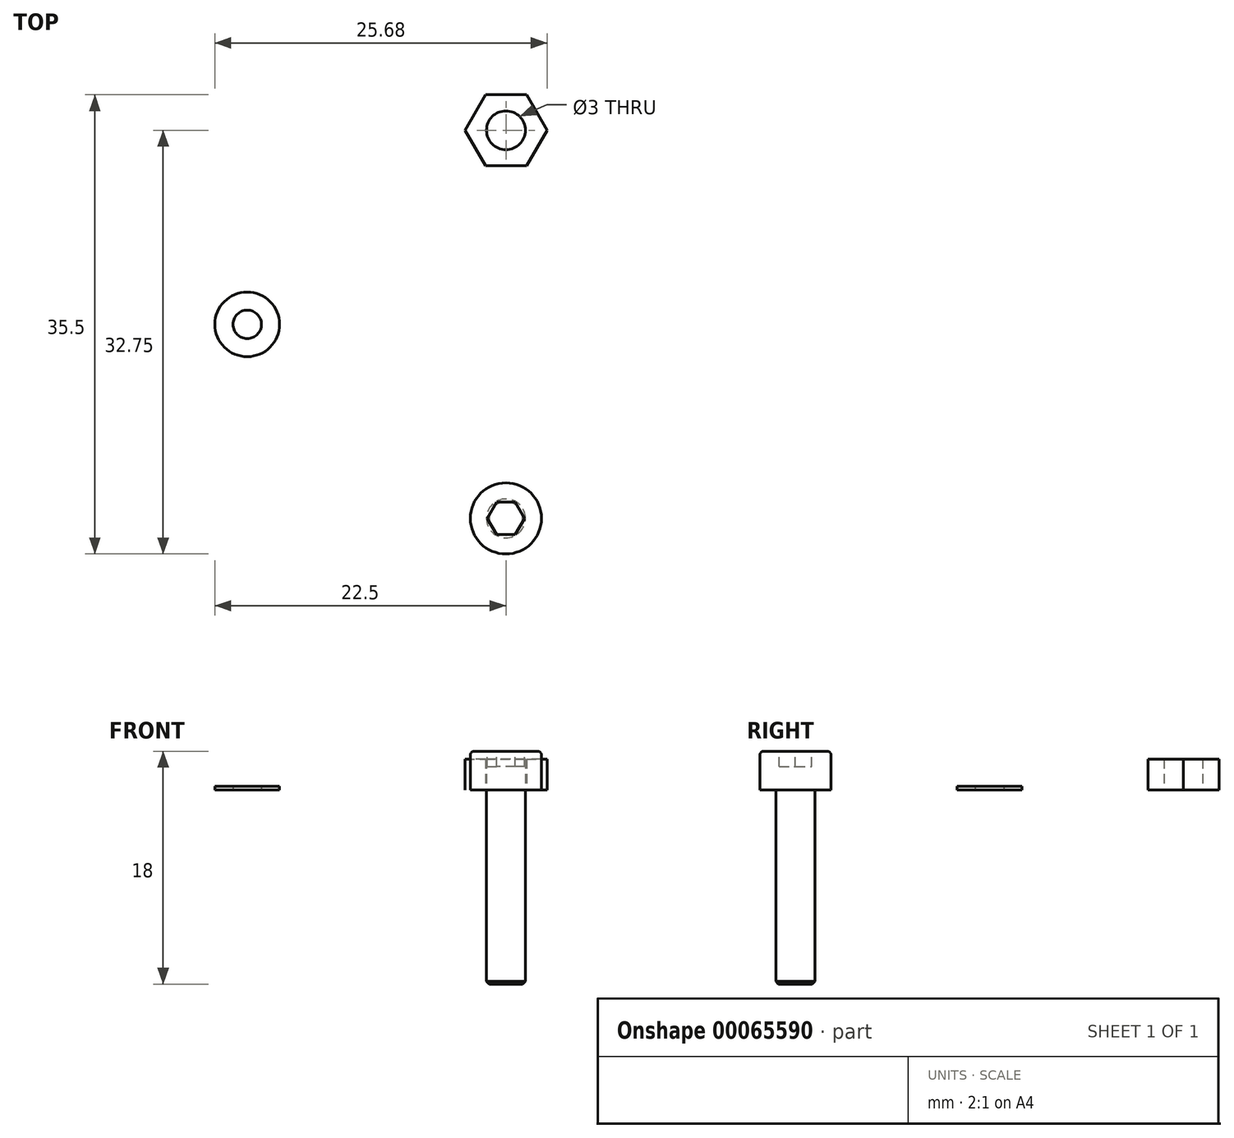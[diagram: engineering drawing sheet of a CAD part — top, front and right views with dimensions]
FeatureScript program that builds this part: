
annotation { "Feature Type Name" : "Feature", "Feature Type Description" : "" }
export const myFeature = defineFeature(function(context is Context, id is Id, definition is map)
    precondition{}
    {
        {
            var Q0;
            Q0=qCreatedBy(makeId("Front.planeOp"),FACE);
            var sketch = newSketch(context, id + "F0", { "sketchPlane" : qUnion([Q0])});
            skLineSegment(sketch, "E0", {"start": v(-10, -10.01) * mm, "end": v(-10, 8.31) * mm, "construction": true});
            skLineSegment(sketch, "E1", {"start": v(-10, 0) * mm, "end": v(-12.75, 0) * mm});
            skLineSegment(sketch, "E2", {"start": v(-12.75, 0) * mm, "end": v(-12.75, 3) * mm});
            skLineSegment(sketch, "E3", {"start": v(-12.75, 3) * mm, "end": v(-10, 3) * mm});
            skLineSegment(sketch, "E4", {"start": v(-10, 3) * mm, "end": v(-10, 0) * mm});
            skLineSegment(sketch, "E5", {"start": v(-10, 0) * mm, "end": v(-10, -15) * mm});
            skLineSegment(sketch, "E6", {"start": v(-10, -15) * mm, "end": v(-11.5, -15) * mm});
            skLineSegment(sketch, "E7", {"start": v(-11.5, -15) * mm, "end": v(-11.5, 0) * mm});
            skSolve(sketch);
        }
        {
            var Q0;
            {var subQ0=sQuery(id+"F0.wireOp",EDGE,"E5");Q0=makeQuery(id+"F0.imprint","IMPRINT",FACE,{"disambiguationData":[TD([[makeQuery(id+"F0.imprint","IMPRINT",EDGE,{"derivedFrom":subQ0}),-1.0]])]});}
            var Q1;
            {var subQ1=sQuery(id+"F0.wireOp",EDGE,"E2");Q1=makeQuery(id+"F0.imprint","IMPRINT",FACE,{"disambiguationData":[TD([[makeQuery(id+"F0.imprint","IMPRINT",EDGE,{"derivedFrom":subQ1}),-1.0]])]});}
            var Q2;
            Q2=sQuery(id+"F0.wireOp",EDGE,"E0");
            revolve(context, id + "F1", {"entities" : qUnion([Q0, Q1]), "axis" : qUnion([Q2]), "revolveType" : RevolveType.FULL});
        }
        {
            var Q0;
            Q0=makeQuery(id+"F1.opRevolve","SWEPT_EDGE",EDGE,{"disambiguationData":[OSD([sQuery(id+"F0.wireOp",EDGE,"E2"),sQuery(id+"F0.wireOp",EDGE,"E3")])]});
            fillet(context, id + "F2", {"entities" : qUnion([Q0]), "radius" : 0.3 * mm, "tangentPropagation" : true, "allowEdgeOverflow" : false});
        }
        {
            var Q0;
            Q0=makeQuery(id+"F1.opRevolve","SWEPT_FACE",FACE,{"disambiguationData":[OSD([sQuery(id+"F0.wireOp",EDGE,"E3")])]});
            var sketch = newSketch(context, id + "F3", { "sketchPlane" : qUnion([Q0])});
            skCircle(sketch, "E8.cCircle", {"center": v(-10, 0) * mm, "radius": 1.25 * mm, "construction": true});
            skLineSegment(sketch, "E8.0", {"start": v(-11.44, 0) * mm, "end": v(-10.72, 1.25) * mm});
            skLineSegment(sketch, "E8.1", {"start": v(-10.72, 1.25) * mm, "end": v(-9.28, 1.25) * mm});
            skLineSegment(sketch, "E8.2", {"start": v(-9.28, 1.25) * mm, "end": v(-8.56, 0) * mm});
            skLineSegment(sketch, "E8.3", {"start": v(-8.56, 0) * mm, "end": v(-9.28, -1.25) * mm});
            skLineSegment(sketch, "E8.4", {"start": v(-9.28, -1.25) * mm, "end": v(-10.72, -1.25) * mm});
            skLineSegment(sketch, "E8.5", {"start": v(-10.72, -1.25) * mm, "end": v(-11.44, 0) * mm});
            skPoint(sketch, "E8.0.midPoint", {"position": v(-11.08, 0.62) * mm});
            skSolve(sketch);
        }
        {
            var Q0;
            Q0=qSketchRegion(id+"F3",true);
            extrude(context, id + "F4", {"entities" : qUnion([Q0]), "operationType" : NewBodyOperationType.REMOVE, "oppositeDirection" : true, "depth" : 1.2 * mm});
        }
        {
            var Q0;
            Q0=makeQuery(id+"F1.opRevolve","SWEPT_EDGE",EDGE,{"disambiguationData":[OSD([sQuery(id+"F0.wireOp",EDGE,"E6"),sQuery(id+"F0.wireOp",EDGE,"E7")])]});
            chamfer(context, id + "F5", {"entities" : qUnion([Q0]), "width" : 0.2 * mm, "tangentPropagation" : true});
        }
        {
            var Q0;
            Q0=qCreatedBy(makeId("Front.planeOp"),FACE);
            var sketch = newSketch(context, id + "F6", { "sketchPlane" : qUnion([Q0])});
            skLineSegment(sketch, "E9", {"start": v(-20, 15.68) * mm, "end": v(-20, -26) * mm, "construction": true});
            skLineSegment(sketch, "E10", {"start": v(-20, 0) * mm, "end": v(-22.25, 0) * mm});
            skLineSegment(sketch, "E11", {"start": v(-22.25, 0) * mm, "end": v(-22.25, 2.5) * mm});
            skLineSegment(sketch, "E12", {"start": v(-22.25, 2.5) * mm, "end": v(-20, 2.5) * mm});
            skLineSegment(sketch, "E13", {"start": v(-20, 2.5) * mm, "end": v(-20, 0) * mm});
            skLineSegment(sketch, "E14", {"start": v(-20, 0) * mm, "end": v(-20, -15) * mm});
            skLineSegment(sketch, "E15", {"start": v(-20, -15) * mm, "end": v(-21.25, -15) * mm});
            skLineSegment(sketch, "E16", {"start": v(-21.25, -15) * mm, "end": v(-21.25, 0) * mm});
            skSolve(sketch);
        }
        {
            var Q0;
            {var subQ1=sQuery(id+"F6.wireOp",EDGE,"E11");Q0=makeQuery(id+"F6.imprint","IMPRINT",FACE,{"disambiguationData":[TD([[makeQuery(id+"F6.imprint","IMPRINT",EDGE,{"derivedFrom":subQ1}),-1.0]])]});}
            var Q1;
            {var subQ1=sQuery(id+"F6.wireOp",EDGE,"E14");Q1=makeQuery(id+"F6.imprint","IMPRINT",FACE,{"disambiguationData":[TD([[makeQuery(id+"F6.imprint","IMPRINT",EDGE,{"derivedFrom":subQ1}),-1.0]])]});}
            var Q2;
            Q2=sQuery(id+"F6.wireOp",EDGE,"E9");
            revolve(context, id + "F7", {"entities" : qUnion([Q0, Q1]), "axis" : qUnion([Q2]), "revolveType" : RevolveType.FULL});
        }
        {
            var Q0;
            Q0=makeQuery(id+"F7.opRevolve","SWEPT_FACE",FACE,{"disambiguationData":[OSD([sQuery(id+"F6.wireOp",EDGE,"E12")])]});
            var sketch = newSketch(context, id + "F8", { "sketchPlane" : qUnion([Q0])});
            skCircle(sketch, "E17.cCircle", {"center": v(-20, 0) * mm, "radius": 1 * mm, "construction": true});
            skLineSegment(sketch, "E17.0", {"start": v(-21.15, 0) * mm, "end": v(-20.58, 1) * mm});
            skLineSegment(sketch, "E17.1", {"start": v(-20.58, 1) * mm, "end": v(-19.42, 1) * mm});
            skLineSegment(sketch, "E17.2", {"start": v(-19.42, 1) * mm, "end": v(-18.85, 0) * mm});
            skLineSegment(sketch, "E17.3", {"start": v(-18.85, 0) * mm, "end": v(-19.42, -1) * mm});
            skLineSegment(sketch, "E17.4", {"start": v(-19.42, -1) * mm, "end": v(-20.58, -1) * mm});
            skLineSegment(sketch, "E17.5", {"start": v(-20.58, -1) * mm, "end": v(-21.15, 0) * mm});
            skPoint(sketch, "E17.0.midPoint", {"position": v(-20.87, 0.5) * mm});
            skSolve(sketch);
        }
        {
            var Q0;
            Q0=qSketchRegion(id+"F8",true);
            extrude(context, id + "F9", {"entities" : qUnion([Q0]), "operationType" : NewBodyOperationType.REMOVE, "oppositeDirection" : true, "depth" : 1.1 * mm});
        }
        {
            var Q0;
            Q0=makeQuery(id+"F7.opRevolve","SWEPT_EDGE",EDGE,{"disambiguationData":[OSD([sQuery(id+"F6.wireOp",EDGE,"E11"),sQuery(id+"F6.wireOp",EDGE,"E12")])]});
            fillet(context, id + "F10", {"entities" : qUnion([Q0]), "radius" : 0.2 * mm, "tangentPropagation" : true, "allowEdgeOverflow" : false});
        }
        {
            var Q0;
            Q0=makeQuery(id+"F7.opRevolve","SWEPT_EDGE",EDGE,{"disambiguationData":[OSD([sQuery(id+"F6.wireOp",EDGE,"E15"),sQuery(id+"F6.wireOp",EDGE,"E16")])]});
            chamfer(context, id + "F11", {"entities" : qUnion([Q0]), "width" : 0.2 * mm, "tangentPropagation" : true});
        }
        {
            var Q0;
            Q0=qCreatedBy(makeId("Front.planeOp"),FACE);
            var sketch = newSketch(context, id + "F12", { "sketchPlane" : qUnion([Q0])});
            skLineSegment(sketch, "E18", {"start": v(-30, 9.47) * mm, "end": v(-30, -21.13) * mm, "construction": true});
            skLineSegment(sketch, "E19", {"start": v(-30, 0) * mm, "end": v(-31.9, 0) * mm});
            skLineSegment(sketch, "E20", {"start": v(-31.9, 0) * mm, "end": v(-31.9, 2) * mm});
            skLineSegment(sketch, "E21", {"start": v(-31.9, 2) * mm, "end": v(-30, 2) * mm});
            skLineSegment(sketch, "E22", {"start": v(-30, 2) * mm, "end": v(-30, 0) * mm});
            skLineSegment(sketch, "E23", {"start": v(-30, 0) * mm, "end": v(-30, -15) * mm});
            skLineSegment(sketch, "E24", {"start": v(-30, -15) * mm, "end": v(-31, -15) * mm});
            skLineSegment(sketch, "E25", {"start": v(-31, -15) * mm, "end": v(-31, 0) * mm});
            skSolve(sketch);
        }
        {
            var Q0;
            Q0=qSketchRegion(id+"F12",true);
            var Q1;
            Q1=sQuery(id+"F12.wireOp",EDGE,"E18");
            revolve(context, id + "F13", {"entities" : qUnion([Q0]), "axis" : qUnion([Q1]), "revolveType" : RevolveType.FULL});
        }
        {
            var Q0;
            Q0=makeQuery(id+"F13.opRevolve","SWEPT_FACE",FACE,{"disambiguationData":[OSD([sQuery(id+"F12.wireOp",EDGE,"E21")])]});
            var sketch = newSketch(context, id + "F14", { "sketchPlane" : qUnion([Q0])});
            skCircle(sketch, "E26.cCircle", {"center": v(-30, 0) * mm, "radius": 1 * mm, "construction": true});
            skLineSegment(sketch, "E26.0", {"start": v(-31.15, 0) * mm, "end": v(-30.58, 1) * mm});
            skLineSegment(sketch, "E26.1", {"start": v(-30.58, 1) * mm, "end": v(-29.42, 1) * mm});
            skLineSegment(sketch, "E26.2", {"start": v(-29.42, 1) * mm, "end": v(-28.85, 0) * mm});
            skLineSegment(sketch, "E26.3", {"start": v(-28.85, 0) * mm, "end": v(-29.42, -1) * mm});
            skLineSegment(sketch, "E26.4", {"start": v(-29.42, -1) * mm, "end": v(-30.58, -1) * mm});
            skLineSegment(sketch, "E26.5", {"start": v(-30.58, -1) * mm, "end": v(-31.15, 0) * mm});
            skPoint(sketch, "E26.0.midPoint", {"position": v(-30.87, 0.5) * mm});
            skSolve(sketch);
        }
        {
            var Q0;
            Q0=qSketchRegion(id+"F14",true);
            extrude(context, id + "F15", {"entities" : qUnion([Q0]), "operationType" : NewBodyOperationType.REMOVE, "oppositeDirection" : true, "depth" : 1 * mm});
        }
        {
            var Q0;
            Q0=makeQuery(id+"F13.opRevolve","SWEPT_EDGE",EDGE,{"disambiguationData":[OSD([sQuery(id+"F12.wireOp",EDGE,"E20"),sQuery(id+"F12.wireOp",EDGE,"E21")])]});
            fillet(context, id + "F16", {"entities" : qUnion([Q0]), "radius" : 0.2 * mm, "tangentPropagation" : true, "allowEdgeOverflow" : false});
        }
        {
            var Q0;
            Q0=makeQuery(id+"F13.opRevolve","SWEPT_EDGE",EDGE,{"disambiguationData":[OSD([sQuery(id+"F12.wireOp",EDGE,"E24"),sQuery(id+"F12.wireOp",EDGE,"E25")])]});
            chamfer(context, id + "F17", {"entities" : qUnion([Q0]), "width" : 0.1 * mm, "tangentPropagation" : true});
        }
        {
            var Q0;
            Q0=qCreatedBy(makeId("Top.planeOp"),FACE);
            var sketch = newSketch(context, id + "F18", { "sketchPlane" : qUnion([Q0])});
            skCircle(sketch, "E27", {"center": v(-10, 15) * mm, "radius": 3.5 * mm});
            skCircle(sketch, "E28", {"center": v(-20, 15) * mm, "radius": 3 * mm});
            skCircle(sketch, "E29", {"center": v(-30, 15) * mm, "radius": 2.5 * mm});
            skLineSegment(sketch, "E30", {"start": v(-30, 15) * mm, "end": v(0, 15) * mm, "construction": true});
            skCircle(sketch, "E31", {"center": v(-30, 15) * mm, "radius": 1.1 * mm});
            skCircle(sketch, "E32", {"center": v(-20, 15) * mm, "radius": 1.35 * mm});
            skCircle(sketch, "E33", {"center": v(-10, 15) * mm, "radius": 1.6 * mm});
            skLineSegment(sketch, "E34", {"start": v(0, 15) * mm, "end": v(10, 15) * mm, "construction": true});
            skCircle(sketch, "E35", {"center": v(10, 15) * mm, "radius": 6 * mm});
            skCircle(sketch, "E36", {"center": v(10, 15) * mm, "radius": 3.2 * mm});
            skSolve(sketch);
        }
        {
            var Q0;
            Q0=makeQuery(id+"F18.imprint","IMPRINT",FACE,{"disambiguationData":[TD([[makeQuery(id+"F18.imprint","IMPRINT",EDGE,{"derivedFrom":sQuery(id+"F18.wireOp",EDGE,"E29")}),1.0]])]});
            extrude(context, id + "F19", {"entities" : qUnion([Q0]), "depth" : 0.3 * mm});
        }
        {
            var Q0;
            Q0=makeQuery(id+"F18.imprint","IMPRINT",FACE,{"disambiguationData":[TD([[makeQuery(id+"F18.imprint","IMPRINT",EDGE,{"derivedFrom":sQuery(id+"F18.wireOp",EDGE,"E28")}),1.0]])]});
            extrude(context, id + "F20", {"entities" : qUnion([Q0]), "depth" : 0.5 * mm});
        }
        {
            var Q0;
            Q0=makeQuery(id+"F18.imprint","IMPRINT",FACE,{"disambiguationData":[TD([[makeQuery(id+"F18.imprint","IMPRINT",EDGE,{"derivedFrom":sQuery(id+"F18.wireOp",EDGE,"E27")}),1.0]])]});
            extrude(context, id + "F21", {"entities" : qUnion([Q0]), "depth" : 0.5 * mm});
        }
        {
            var Q0;
            Q0=qCreatedBy(makeId("Top.planeOp"),FACE);
            var sketch = newSketch(context, id + "F22", { "sketchPlane" : qUnion([Q0])});
            skLineSegment(sketch, "E37", {"start": v(0, 30) * mm, "end": v(-30, 30) * mm, "construction": true});
            skCircle(sketch, "E38.cCircle", {"center": v(-10, 30) * mm, "radius": 2.75 * mm, "construction": true});
            skLineSegment(sketch, "E38.0", {"start": v(-11.59, 32.75) * mm, "end": v(-8.41, 32.75) * mm});
            skLineSegment(sketch, "E38.1", {"start": v(-8.41, 32.75) * mm, "end": v(-6.82, 30) * mm});
            skLineSegment(sketch, "E38.2", {"start": v(-6.82, 30) * mm, "end": v(-8.41, 27.25) * mm});
            skLineSegment(sketch, "E38.3", {"start": v(-8.41, 27.25) * mm, "end": v(-11.59, 27.25) * mm});
            skLineSegment(sketch, "E38.4", {"start": v(-11.59, 27.25) * mm, "end": v(-13.18, 30) * mm});
            skLineSegment(sketch, "E38.5", {"start": v(-13.18, 30) * mm, "end": v(-11.59, 32.75) * mm});
            skPoint(sketch, "E38.0.midPoint", {"position": v(-10, 32.75) * mm});
            skCircle(sketch, "E39.cCircle", {"center": v(-20, 30) * mm, "radius": 2.5 * mm, "construction": true});
            skLineSegment(sketch, "E39.0", {"start": v(-21.44, 32.5) * mm, "end": v(-18.56, 32.5) * mm});
            skLineSegment(sketch, "E39.1", {"start": v(-18.56, 32.5) * mm, "end": v(-17.11, 30) * mm});
            skLineSegment(sketch, "E39.2", {"start": v(-17.11, 30) * mm, "end": v(-18.56, 27.5) * mm});
            skLineSegment(sketch, "E39.3", {"start": v(-18.56, 27.5) * mm, "end": v(-21.44, 27.5) * mm});
            skLineSegment(sketch, "E39.4", {"start": v(-21.44, 27.5) * mm, "end": v(-22.89, 30) * mm});
            skLineSegment(sketch, "E39.5", {"start": v(-22.89, 30) * mm, "end": v(-21.44, 32.5) * mm});
            skPoint(sketch, "E39.0.midPoint", {"position": v(-20, 32.5) * mm});
            skCircle(sketch, "E40.cCircle", {"center": v(-30, 30) * mm, "radius": 2 * mm, "construction": true});
            skLineSegment(sketch, "E40.0", {"start": v(-31.15, 32) * mm, "end": v(-28.85, 32) * mm});
            skLineSegment(sketch, "E40.1", {"start": v(-28.85, 32) * mm, "end": v(-27.7, 30) * mm});
            skLineSegment(sketch, "E40.2", {"start": v(-27.7, 30) * mm, "end": v(-28.85, 28) * mm});
            skLineSegment(sketch, "E40.3", {"start": v(-28.85, 28) * mm, "end": v(-31.15, 28) * mm});
            skLineSegment(sketch, "E40.4", {"start": v(-31.15, 28) * mm, "end": v(-32.3, 30) * mm});
            skLineSegment(sketch, "E40.5", {"start": v(-32.3, 30) * mm, "end": v(-31.15, 32) * mm});
            skPoint(sketch, "E40.0.midPoint", {"position": v(-30, 32) * mm});
            skCircle(sketch, "E41", {"center": v(-30, 30) * mm, "radius": 1 * mm});
            skCircle(sketch, "E42", {"center": v(-20, 30) * mm, "radius": 1.25 * mm});
            skCircle(sketch, "E43", {"center": v(-10, 30) * mm, "radius": 1.5 * mm});
            skLineSegment(sketch, "E44", {"start": v(0, 30) * mm, "end": v(10, 30) * mm, "construction": true});
            skCircle(sketch, "E45.cCircle", {"center": v(10, 30) * mm, "radius": 5 * mm, "construction": true});
            skLineSegment(sketch, "E45.0", {"start": v(7.11, 35) * mm, "end": v(12.89, 35) * mm});
            skLineSegment(sketch, "E45.1", {"start": v(12.89, 35) * mm, "end": v(15.77, 30) * mm});
            skLineSegment(sketch, "E45.2", {"start": v(15.77, 30) * mm, "end": v(12.89, 25) * mm});
            skLineSegment(sketch, "E45.3", {"start": v(12.89, 25) * mm, "end": v(7.11, 25) * mm});
            skLineSegment(sketch, "E45.4", {"start": v(7.11, 25) * mm, "end": v(4.23, 30) * mm});
            skLineSegment(sketch, "E45.5", {"start": v(4.23, 30) * mm, "end": v(7.11, 35) * mm});
            skPoint(sketch, "E45.0.midPoint", {"position": v(10, 35) * mm});
            skCircle(sketch, "E46", {"center": v(10, 30) * mm, "radius": 3 * mm});
            skSolve(sketch);
        }
        {
            var Q0;
            Q0=makeQuery(id+"F22.imprint","IMPRINT",FACE,{"disambiguationData":[TD([[makeQuery(id+"F22.imprint","IMPRINT",EDGE,{"derivedFrom":sQuery(id+"F22.wireOp",EDGE,"E40.0")}),-1.0]])]});
            extrude(context, id + "F23", {"entities" : qUnion([Q0]), "depth" : 1.6 * mm});
        }
        {
            var Q0;
            Q0=makeQuery(id+"F22.imprint","IMPRINT",FACE,{"disambiguationData":[TD([[makeQuery(id+"F22.imprint","IMPRINT",EDGE,{"derivedFrom":sQuery(id+"F22.wireOp",EDGE,"E39.0")}),-1.0]])]});
            extrude(context, id + "F24", {"entities" : qUnion([Q0]), "depth" : 2 * mm});
        }
        {
            var Q0;
            Q0=makeQuery(id+"F22.imprint","IMPRINT",FACE,{"disambiguationData":[TD([[makeQuery(id+"F22.imprint","IMPRINT",EDGE,{"derivedFrom":sQuery(id+"F22.wireOp",EDGE,"E38.0")}),-1.0]])]});
            extrude(context, id + "F25", {"entities" : qUnion([Q0]), "depth" : 2.4 * mm});
        }
        {
            var Q0;
            Q0=qCreatedBy(makeId("Front.planeOp"),FACE);
            var sketch = newSketch(context, id + "F26", { "sketchPlane" : qUnion([Q0])});
            skLineSegment(sketch, "E47", {"start": v(8.39, -9.9) * mm, "end": v(8.39, 8.44) * mm, "construction": true});
            skLineSegment(sketch, "E48", {"start": v(8.39, 0.12) * mm, "end": v(3.39, 0.12) * mm});
            skLineSegment(sketch, "E49", {"start": v(3.39, 0.12) * mm, "end": v(3.39, 6.12) * mm});
            skLineSegment(sketch, "E50", {"start": v(3.39, 6.12) * mm, "end": v(8.39, 6.12) * mm});
            skLineSegment(sketch, "E51", {"start": v(8.39, 6.12) * mm, "end": v(8.39, 0.12) * mm});
            skLineSegment(sketch, "E52", {"start": v(8.39, 0.12) * mm, "end": v(8.39, -24.88) * mm});
            skLineSegment(sketch, "E53", {"start": v(8.39, -24.88) * mm, "end": v(5.39, -24.88) * mm});
            skLineSegment(sketch, "E54", {"start": v(5.39, -24.88) * mm, "end": v(5.39, 0.12) * mm});
            skSolve(sketch);
        }
        {
            var Q0;
            Q0=qSketchRegion(id+"F26",true);
            var Q1;
            Q1=sQuery(id+"F26.wireOp",EDGE,"E47");
            revolve(context, id + "F27", {"entities" : qUnion([Q0]), "axis" : qUnion([Q1]), "revolveType" : RevolveType.FULL});
        }
        {
            var Q0;
            Q0=makeQuery(id+"F27.opRevolve","SWEPT_FACE",FACE,{"disambiguationData":[OSD([sQuery(id+"F26.wireOp",EDGE,"E50")])]});
            var sketch = newSketch(context, id + "F28", { "sketchPlane" : qUnion([Q0])});
            skCircle(sketch, "E55.cCircle", {"center": v(8.39, 0) * mm, "radius": 2.5 * mm, "construction": true});
            skLineSegment(sketch, "E55.0", {"start": v(10.89, 1.44) * mm, "end": v(10.89, -1.44) * mm});
            skLineSegment(sketch, "E55.1", {"start": v(10.89, -1.44) * mm, "end": v(8.39, -2.89) * mm});
            skLineSegment(sketch, "E55.2", {"start": v(8.39, -2.89) * mm, "end": v(5.89, -1.44) * mm});
            skLineSegment(sketch, "E55.3", {"start": v(5.89, -1.44) * mm, "end": v(5.89, 1.44) * mm});
            skLineSegment(sketch, "E55.4", {"start": v(5.89, 1.44) * mm, "end": v(8.39, 2.89) * mm});
            skLineSegment(sketch, "E55.5", {"start": v(8.39, 2.89) * mm, "end": v(10.89, 1.44) * mm});
            skPoint(sketch, "E55.0.midPoint", {"position": v(10.89, 0) * mm});
            skSolve(sketch);
        }
        {
            var Q0;
            Q0=qSketchRegion(id+"F28",true);
            extrude(context, id + "F29", {"entities" : qUnion([Q0]), "operationType" : NewBodyOperationType.REMOVE, "oppositeDirection" : true, "depth" : 3 * mm});
        }
        {
            var Q0;
            Q0=makeQuery(id+"F18.imprint","IMPRINT",FACE,{"disambiguationData":[TD([[makeQuery(id+"F18.imprint","IMPRINT",EDGE,{"derivedFrom":sQuery(id+"F18.wireOp",EDGE,"E35")}),1.0]])]});
            extrude(context, id + "F30", {"entities" : qUnion([Q0]), "depth" : 1.4 * mm});
        }
        {
            var Q0;
            Q0=makeQuery(id+"F22.imprint","IMPRINT",FACE,{"disambiguationData":[TD([[makeQuery(id+"F22.imprint","IMPRINT",EDGE,{"derivedFrom":sQuery(id+"F22.wireOp",EDGE,"E45.0")}),-1.0]])]});
            extrude(context, id + "F31", {"entities" : qUnion([Q0]), "depth" : 5 * mm});
        }
        {
            var Q0;
            Q0=makeQuery(id+"F7.opRevolve","SWEPT_BODY",BODY,{"disambiguationData":[OSD([sQuery(id+"F6.wireOp",EDGE,"E10"),sQuery(id+"F6.wireOp",EDGE,"E11"),sQuery(id+"F6.wireOp",EDGE,"E12"),sQuery(id+"F6.wireOp",EDGE,"E13"),sQuery(id+"F6.wireOp",EDGE,"E14"),sQuery(id+"F6.wireOp",EDGE,"E15"),sQuery(id+"F6.wireOp",EDGE,"E16")])]});
            var Q1;
            Q1=makeQuery(id+"F13.opRevolve","SWEPT_BODY",BODY,{"disambiguationData":[OSD([sQuery(id+"F12.wireOp",EDGE,"E19"),sQuery(id+"F12.wireOp",EDGE,"E20"),sQuery(id+"F12.wireOp",EDGE,"E21"),sQuery(id+"F12.wireOp",EDGE,"E22"),sQuery(id+"F12.wireOp",EDGE,"E23"),sQuery(id+"F12.wireOp",EDGE,"E24"),sQuery(id+"F12.wireOp",EDGE,"E25")])]});
            deleteBodies(context, id + "F32", {"entities" : qUnion([Q0, Q1])});
        }
        {
            var Q0;
            Q0=makeQuery(id+"F21.opExtrude","SWEPT_BODY",BODY,{"disambiguationData":[OSD([sQuery(id+"F18.wireOp",EDGE,"E27"),sQuery(id+"F18.wireOp",EDGE,"E33")])]});
            deleteBodies(context, id + "F33", {"entities" : qUnion([Q0])});
        }
        {
            var Q0;
            Q0=makeQuery(id+"F20.opExtrude","SWEPT_BODY",BODY,{"disambiguationData":[OSD([sQuery(id+"F18.wireOp",EDGE,"E28"),sQuery(id+"F18.wireOp",EDGE,"E32")])]});
            var Q1;
            Q1=makeQuery(id+"F24.opExtrude","SWEPT_BODY",BODY,{"disambiguationData":[OSD([sQuery(id+"F22.wireOp",EDGE,"E39.0"),sQuery(id+"F22.wireOp",EDGE,"E39.1"),sQuery(id+"F22.wireOp",EDGE,"E39.2"),sQuery(id+"F22.wireOp",EDGE,"E39.3"),sQuery(id+"F22.wireOp",EDGE,"E39.4"),sQuery(id+"F22.wireOp",EDGE,"E39.5"),sQuery(id+"F22.wireOp",EDGE,"E42")])]});
            deleteBodies(context, id + "F34", {"entities" : qUnion([Q0, Q1])});
        }
        {
            var Q0;
            Q0=makeQuery(id+"F23.opExtrude","SWEPT_BODY",BODY,{"disambiguationData":[OSD([sQuery(id+"F22.wireOp",EDGE,"E40.0"),sQuery(id+"F22.wireOp",EDGE,"E40.1"),sQuery(id+"F22.wireOp",EDGE,"E40.2"),sQuery(id+"F22.wireOp",EDGE,"E40.3"),sQuery(id+"F22.wireOp",EDGE,"E40.4"),sQuery(id+"F22.wireOp",EDGE,"E40.5"),sQuery(id+"F22.wireOp",EDGE,"E41")])]});
            var Q1;
            Q1=makeQuery(id+"F27.opRevolve","SWEPT_BODY",BODY,{"disambiguationData":[OSD([sQuery(id+"F26.wireOp",EDGE,"E48"),sQuery(id+"F26.wireOp",EDGE,"E49"),sQuery(id+"F26.wireOp",EDGE,"E50"),sQuery(id+"F26.wireOp",EDGE,"E51"),sQuery(id+"F26.wireOp",EDGE,"E52"),sQuery(id+"F26.wireOp",EDGE,"E53"),sQuery(id+"F26.wireOp",EDGE,"E54")])]});
            var Q2;
            Q2=makeQuery(id+"F31.opExtrude","SWEPT_BODY",BODY,{"disambiguationData":[OSD([sQuery(id+"F22.wireOp",EDGE,"E45.0"),sQuery(id+"F22.wireOp",EDGE,"E45.1"),sQuery(id+"F22.wireOp",EDGE,"E45.2"),sQuery(id+"F22.wireOp",EDGE,"E45.3"),sQuery(id+"F22.wireOp",EDGE,"E45.4"),sQuery(id+"F22.wireOp",EDGE,"E45.5"),sQuery(id+"F22.wireOp",EDGE,"E46")])]});
            var Q3;
            Q3=makeQuery(id+"F30.opExtrude","SWEPT_BODY",BODY,{"disambiguationData":[OSD([sQuery(id+"F18.wireOp",EDGE,"E35"),sQuery(id+"F18.wireOp",EDGE,"E36")])]});
            deleteBodies(context, id + "F35", {"entities" : qUnion([Q0, Q1, Q2, Q3])});
        }
    });
